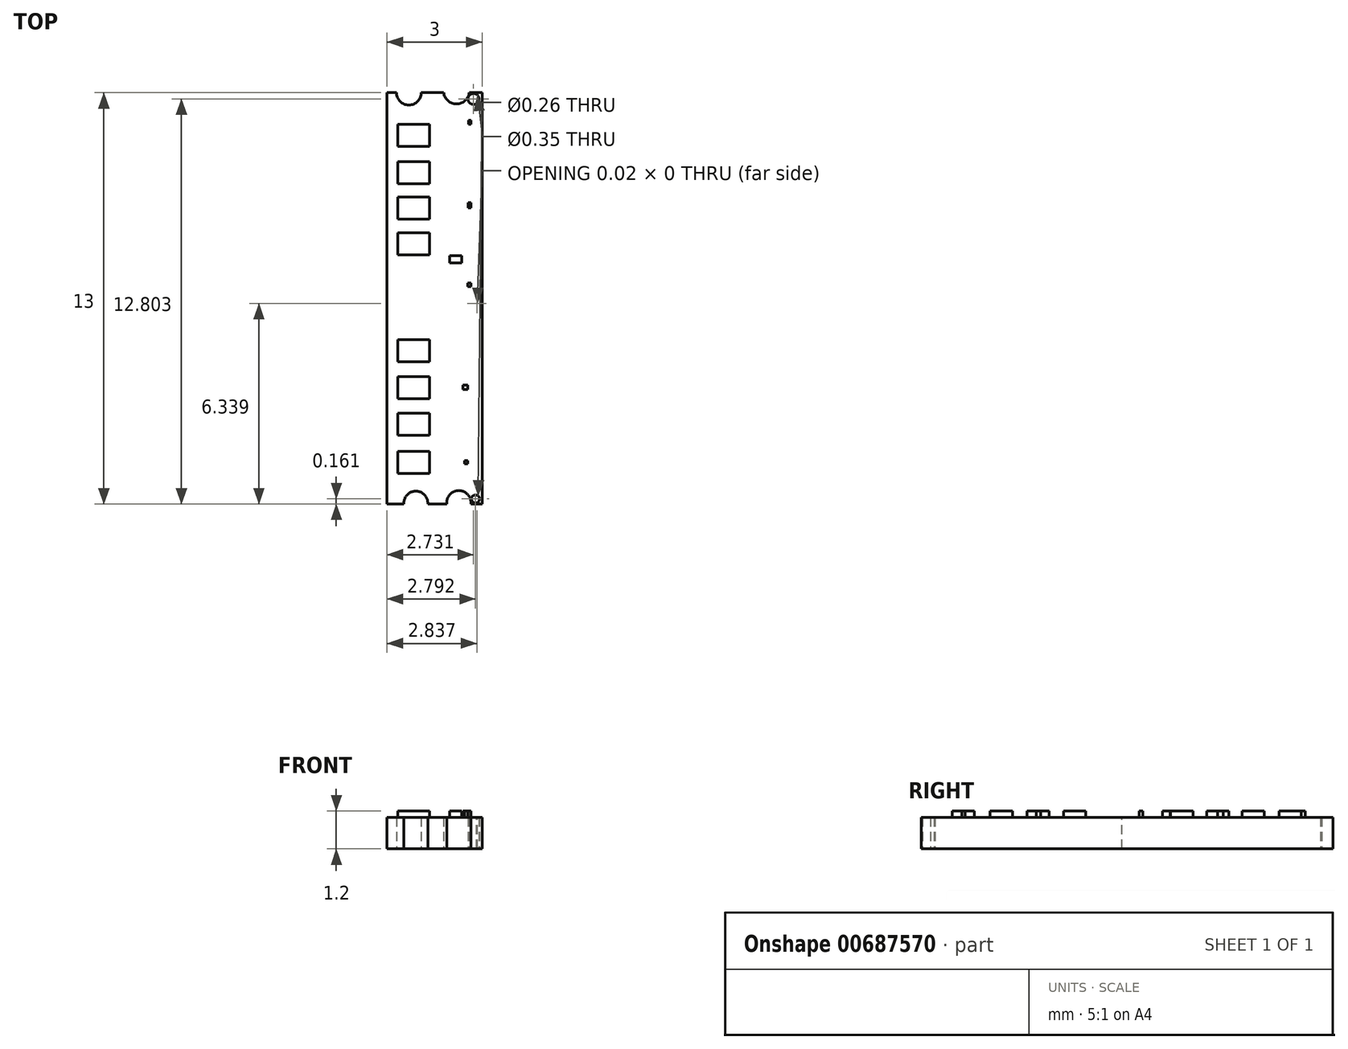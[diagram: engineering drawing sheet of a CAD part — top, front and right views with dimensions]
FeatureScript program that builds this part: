
annotation { "Feature Type Name" : "Feature", "Feature Type Description" : "" }
export const myFeature = defineFeature(function(context is Context, id is Id, definition is map)
    precondition{}
    {
        {
            var Q0;
            Q0=qCreatedBy(makeId("Top.planeOp"),FACE);
            var sketch = newSketch(context, id + "F0", { "sketchPlane" : qUnion([Q0])});
            skLineSegment(sketch, "E0.bottom", {"start": v(-25.2, -49.3) * mm, "end": v(-24.9, -49.3) * mm});
            skLineSegment(sketch, "E0.top", {"start": v(-25.2, -62.3) * mm, "end": v(-24.67, -62.3) * mm});
            skLineSegment(sketch, "E0.left", {"start": v(-25.2, -49.3) * mm, "end": v(-25.2, -62.3) * mm});
            skLineSegment(sketch, "E0.right", {"start": v(-22.2, -49.3) * mm, "end": v(-22.2, -62.3) * mm});
            skArc(sketch, "E1", {"start": v(-24.9, -49.3) * mm, "mid": v(-24.51, -49.69) * mm, "end": v(-24.12, -49.3) * mm});
            skLineSegment(sketch, "E2.trimOffspring", {"start": v(-24.12, -49.3) * mm, "end": v(-23.41, -49.3) * mm});
            skLineSegment(sketch, "E3.trimOffspring", {"start": v(-22.6, -49.3) * mm, "end": v(-22.2, -49.3) * mm});
            skArc(sketch, "E4", {"start": v(-23.91, -62.3) * mm, "mid": v(-24.3, -61.9) * mm, "end": v(-24.67, -62.3) * mm});
            skArc(sketch, "E5", {"start": v(-22.56, -62.3) * mm, "mid": v(-22.94, -61.87) * mm, "end": v(-23.31, -62.3) * mm});
            skLineSegment(sketch, "E6.trimOffspring", {"start": v(-23.91, -62.3) * mm, "end": v(-23.31, -62.3) * mm});
            skLineSegment(sketch, "E7.trimOffspring", {"start": v(-22.56, -62.3) * mm, "end": v(-22.2, -62.3) * mm});
            skArc(sketch, "E8", {"start": v(-23.41, -49.3) * mm, "mid": v(-23, -49.66) * mm, "end": v(-22.6, -49.3) * mm});
            skSolve(sketch);
        }
        {
            var Q0;
            Q0 = qSketchRegion(id + "F0", true);
            extrude(context, id + "F1", {"entities" : qUnion([Q0]), "depth" : 1 * mm, "offsetDistance" : 25 * mm});
        }
        {
            var Q0;
            Q0=qCreatedBy(makeId("Top.planeOp"),FACE);
            var sketch = newSketch(context, id + "F2", { "sketchPlane" : qUnion([Q0])});
            skCircle(sketch, "E9", {"center": v(-22.47, -49.5) * mm, "radius": 0.17 * mm});
            skCircle(sketch, "E10", {"center": v(-22.4, -62.14) * mm, "radius": 0.13 * mm});
            skSolve(sketch);
        }
        {
            var Q0;
            Q0 = qSketchRegion(id + "F2", true);
            extrude(context, id + "F3", {"entities" : qUnion([Q0]), "operationType" : NewBodyOperationType.REMOVE, "endBound" : BoundingType.THROUGH_ALL, "depth" : 1 * mm, "offsetDistance" : 25 * mm});
        }
        {
            var Q0;
            Q0=makeQuery(id+"F1.opExtrude","CAP_FACE",FACE,{"disambiguationData":[OSD([sQuery(id+"F0.wireOp",EDGE,"E0.bottom"),sQuery(id+"F0.wireOp",EDGE,"E0.top"),sQuery(id+"F0.wireOp",EDGE,"E0.left"),sQuery(id+"F0.wireOp",EDGE,"E0.right"),sQuery(id+"F0.wireOp",EDGE,"E1"),sQuery(id+"F0.wireOp",EDGE,"E2.trimOffspring"),sQuery(id+"F0.wireOp",EDGE,"E3.trimOffspring"),sQuery(id+"F0.wireOp",EDGE,"E4"),sQuery(id+"F0.wireOp",EDGE,"E5"),sQuery(id+"F0.wireOp",EDGE,"E6.trimOffspring"),sQuery(id+"F0.wireOp",EDGE,"E7.trimOffspring"),sQuery(id+"F0.wireOp",EDGE,"E8")])],"isStart":false});
            var sketch = newSketch(context, id + "F4", { "sketchPlane" : qUnion([Q0])});
            skLineSegment(sketch, "E11.bottom", {"start": v(-24.86, -50.3) * mm, "end": v(-23.86, -50.3) * mm});
            skLineSegment(sketch, "E11.top", {"start": v(-24.86, -51) * mm, "end": v(-23.86, -51) * mm});
            skLineSegment(sketch, "E11.left", {"start": v(-24.86, -50.3) * mm, "end": v(-24.86, -51) * mm});
            skLineSegment(sketch, "E11.right", {"start": v(-23.86, -50.3) * mm, "end": v(-23.86, -51) * mm});
            skLineSegment(sketch, "E12.bottom", {"start": v(-24.86, -51.47) * mm, "end": v(-23.86, -51.47) * mm});
            skLineSegment(sketch, "E12.top", {"start": v(-24.86, -52.17) * mm, "end": v(-23.86, -52.17) * mm});
            skLineSegment(sketch, "E12.left", {"start": v(-24.86, -51.47) * mm, "end": v(-24.86, -52.17) * mm});
            skLineSegment(sketch, "E12.right", {"start": v(-23.86, -51.47) * mm, "end": v(-23.86, -52.17) * mm});
            skLineSegment(sketch, "E13.bottom", {"start": v(-24.86, -52.6) * mm, "end": v(-23.86, -52.6) * mm});
            skLineSegment(sketch, "E13.top", {"start": v(-24.86, -53.3) * mm, "end": v(-23.86, -53.3) * mm});
            skLineSegment(sketch, "E13.left", {"start": v(-24.86, -52.6) * mm, "end": v(-24.86, -53.3) * mm});
            skLineSegment(sketch, "E13.right", {"start": v(-23.86, -52.6) * mm, "end": v(-23.86, -53.3) * mm});
            skLineSegment(sketch, "E14.bottom", {"start": v(-24.86, -53.72) * mm, "end": v(-23.86, -53.72) * mm});
            skLineSegment(sketch, "E14.top", {"start": v(-24.86, -54.42) * mm, "end": v(-23.86, -54.42) * mm});
            skLineSegment(sketch, "E14.left", {"start": v(-24.86, -53.72) * mm, "end": v(-24.86, -54.42) * mm});
            skLineSegment(sketch, "E14.right", {"start": v(-23.86, -53.72) * mm, "end": v(-23.86, -54.42) * mm});
            skLineSegment(sketch, "E15.bottom", {"start": v(-23.23, -54.44) * mm, "end": v(-22.85, -54.44) * mm});
            skLineSegment(sketch, "E15.top", {"start": v(-23.23, -54.68) * mm, "end": v(-22.85, -54.68) * mm});
            skLineSegment(sketch, "E15.left", {"start": v(-23.23, -54.44) * mm, "end": v(-23.23, -54.68) * mm});
            skLineSegment(sketch, "E15.right", {"start": v(-22.85, -54.44) * mm, "end": v(-22.85, -54.68) * mm});
            skLineSegment(sketch, "E16.bottom", {"start": v(-24.86, -61.33) * mm, "end": v(-23.86, -61.33) * mm});
            skLineSegment(sketch, "E16.top", {"start": v(-24.86, -60.63) * mm, "end": v(-23.86, -60.63) * mm});
            skLineSegment(sketch, "E16.left", {"start": v(-24.86, -61.33) * mm, "end": v(-24.86, -60.63) * mm});
            skLineSegment(sketch, "E16.right", {"start": v(-23.86, -61.33) * mm, "end": v(-23.86, -60.63) * mm});
            skLineSegment(sketch, "E17.bottom", {"start": v(-24.86, -60.13) * mm, "end": v(-23.86, -60.13) * mm});
            skLineSegment(sketch, "E17.top", {"start": v(-24.86, -59.43) * mm, "end": v(-23.86, -59.43) * mm});
            skLineSegment(sketch, "E17.left", {"start": v(-24.86, -60.13) * mm, "end": v(-24.86, -59.43) * mm});
            skLineSegment(sketch, "E17.right", {"start": v(-23.86, -60.13) * mm, "end": v(-23.86, -59.43) * mm});
            skLineSegment(sketch, "E18.bottom", {"start": v(-24.86, -58.97) * mm, "end": v(-23.86, -58.97) * mm});
            skLineSegment(sketch, "E18.top", {"start": v(-24.86, -58.27) * mm, "end": v(-23.86, -58.27) * mm});
            skLineSegment(sketch, "E18.left", {"start": v(-24.86, -58.97) * mm, "end": v(-24.86, -58.27) * mm});
            skLineSegment(sketch, "E18.right", {"start": v(-23.86, -58.97) * mm, "end": v(-23.86, -58.27) * mm});
            skLineSegment(sketch, "E19.bottom", {"start": v(-24.86, -57.8) * mm, "end": v(-23.86, -57.8) * mm});
            skLineSegment(sketch, "E19.top", {"start": v(-24.86, -57.1) * mm, "end": v(-23.86, -57.1) * mm});
            skLineSegment(sketch, "E19.left", {"start": v(-24.86, -57.8) * mm, "end": v(-24.86, -57.1) * mm});
            skLineSegment(sketch, "E19.right", {"start": v(-23.86, -57.8) * mm, "end": v(-23.86, -57.1) * mm});
            skSolve(sketch);
        }
        {
            var Q0;
            Q0 = qSketchRegion(id + "F4", true);
            extrude(context, id + "F5", {"entities" : qUnion([Q0]), "operationType" : NewBodyOperationType.ADD, "depth" : 0.2 * mm, "offsetDistance" : 25 * mm});
        }
        {
            var Q0;
            Q0=makeQuery(id+"F1.opExtrude","CAP_FACE",FACE,{"disambiguationData":[OSD([sQuery(id+"F0.wireOp",EDGE,"E0.bottom"),sQuery(id+"F0.wireOp",EDGE,"E0.top"),sQuery(id+"F0.wireOp",EDGE,"E0.left"),sQuery(id+"F0.wireOp",EDGE,"E0.right"),sQuery(id+"F0.wireOp",EDGE,"E1"),sQuery(id+"F0.wireOp",EDGE,"E2.trimOffspring"),sQuery(id+"F0.wireOp",EDGE,"E3.trimOffspring"),sQuery(id+"F0.wireOp",EDGE,"E4"),sQuery(id+"F0.wireOp",EDGE,"E5"),sQuery(id+"F0.wireOp",EDGE,"E6.trimOffspring"),sQuery(id+"F0.wireOp",EDGE,"E7.trimOffspring"),sQuery(id+"F0.wireOp",EDGE,"E8")])],"isStart":false});
            var sketch = newSketch(context, id + "F6", { "sketchPlane" : qUnion([Q0])});
            skArc(sketch, "E20", {"start": v(-22.36, -55.63) * mm, "mid": v(-22.53, -55.8) * mm, "end": v(-22.35, -55.96) * mm});
            skPoint(sketch, "E20.centerSnap0", {"position": v(-22.2, -55.8) * mm});
            skLineSegment(sketch, "E21", {"start": v(-22.37, -55.96) * mm, "end": v(-22.2, -55.96) * mm});
            skLineSegment(sketch, "E22", {"start": v(-22.36, -55.63) * mm, "end": v(-22.2, -55.63) * mm});
            skSolve(sketch);
        }
        {
            var Q0;
            Q0 = qSketchRegion(id + "F6", true);
            var Q1;
            {var subQ5=sQuery(id+"F6.wireOp",EDGE,"E20");Q1=makeQuery(id+"F6.imprint","IMPRINT",FACE,{"disambiguationData":[TD([[makeQuery(id+"F6.imprint","IMPRINT",EDGE,{"derivedFrom":subQ5}),1.0]])]});}
            extrude(context, id + "F7", {"entities" : qUnion([Q0, Q1]), "operationType" : NewBodyOperationType.REMOVE, "endBound" : BoundingType.THROUGH_ALL, "oppositeDirection" : true, "depth" : 25 * mm, "offsetDistance" : 25 * mm});
        }
        {
            var Q0;
            Q0=makeQuery(id+"F1.opExtrude","CAP_FACE",FACE,{"disambiguationData":[OSD([sQuery(id+"F0.wireOp",EDGE,"E0.bottom"),sQuery(id+"F0.wireOp",EDGE,"E0.top"),sQuery(id+"F0.wireOp",EDGE,"E0.left"),sQuery(id+"F0.wireOp",EDGE,"E0.right"),sQuery(id+"F0.wireOp",EDGE,"E1"),sQuery(id+"F0.wireOp",EDGE,"E2.trimOffspring"),sQuery(id+"F0.wireOp",EDGE,"E3.trimOffspring"),sQuery(id+"F0.wireOp",EDGE,"E4"),sQuery(id+"F0.wireOp",EDGE,"E5"),sQuery(id+"F0.wireOp",EDGE,"E6.trimOffspring"),sQuery(id+"F0.wireOp",EDGE,"E7.trimOffspring"),sQuery(id+"F0.wireOp",EDGE,"E8")])],"isStart":false});
            var sketch = newSketch(context, id + "F8", { "sketchPlane" : qUnion([Q0])});
            skLineSegment(sketch, "E23.bottom", {"start": v(-22.62, -50.3) * mm, "end": v(-22.55, -50.3) * mm});
            skLineSegment(sketch, "E23.top", {"start": v(-22.62, -50.17) * mm, "end": v(-22.55, -50.17) * mm});
            skLineSegment(sketch, "E23.left", {"start": v(-22.62, -50.3) * mm, "end": v(-22.62, -50.17) * mm});
            skLineSegment(sketch, "E23.right", {"start": v(-22.55, -50.3) * mm, "end": v(-22.55, -50.17) * mm});
            skPoint(sketch, "E24.firstSnap0", {"position": v(-23.86, -52.94) * mm});
            skLineSegment(sketch, "E24.bottom", {"start": v(-22.55, -52.94) * mm, "end": v(-22.65, -52.94) * mm});
            skLineSegment(sketch, "E24.top", {"start": v(-22.55, -52.77) * mm, "end": v(-22.65, -52.77) * mm});
            skLineSegment(sketch, "E24.left", {"start": v(-22.55, -52.94) * mm, "end": v(-22.55, -52.77) * mm});
            skLineSegment(sketch, "E24.right", {"start": v(-22.65, -52.94) * mm, "end": v(-22.65, -52.77) * mm});
            skLineSegment(sketch, "E25.bottom", {"start": v(-22.55, -55.42) * mm, "end": v(-22.66, -55.42) * mm});
            skLineSegment(sketch, "E25.top", {"start": v(-22.55, -55.31) * mm, "end": v(-22.66, -55.31) * mm});
            skLineSegment(sketch, "E25.left", {"start": v(-22.55, -55.42) * mm, "end": v(-22.55, -55.31) * mm});
            skLineSegment(sketch, "E25.right", {"start": v(-22.66, -55.42) * mm, "end": v(-22.66, -55.31) * mm});
            skLineSegment(sketch, "E26.bottom", {"start": v(-22.66, -61.03) * mm, "end": v(-22.76, -61.03) * mm});
            skLineSegment(sketch, "E26.top", {"start": v(-22.66, -60.92) * mm, "end": v(-22.76, -60.92) * mm});
            skLineSegment(sketch, "E26.left", {"start": v(-22.66, -61.03) * mm, "end": v(-22.66, -60.92) * mm});
            skLineSegment(sketch, "E26.right", {"start": v(-22.76, -61.03) * mm, "end": v(-22.76, -60.92) * mm});
            skLineSegment(sketch, "E27.bottom", {"start": v(-22.66, -58.67) * mm, "end": v(-22.8, -58.67) * mm});
            skLineSegment(sketch, "E27.top", {"start": v(-22.66, -58.53) * mm, "end": v(-22.8, -58.53) * mm});
            skLineSegment(sketch, "E27.left", {"start": v(-22.66, -58.67) * mm, "end": v(-22.66, -58.53) * mm});
            skLineSegment(sketch, "E27.right", {"start": v(-22.8, -58.67) * mm, "end": v(-22.8, -58.53) * mm});
            skSolve(sketch);
        }
        {
            var Q0;
            Q0 = qSketchRegion(id + "F8", true);
            extrude(context, id + "F9", {"entities" : qUnion([Q0]), "operationType" : NewBodyOperationType.ADD, "depth" : 0.2 * mm, "offsetDistance" : 25 * mm});
        }
    });
